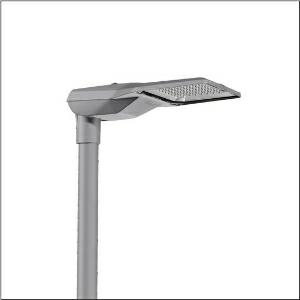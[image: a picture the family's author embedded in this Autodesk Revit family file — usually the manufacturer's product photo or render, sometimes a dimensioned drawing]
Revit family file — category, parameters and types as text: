
# Revit family: streetlight_sl_21_midi___stw1_0a_5xe3e43s08lb_9506
name_source: partatom
category: Lighting Fixtures
units: mm (PartAtom-declared; Revit-internal decimal feet)

## family parameters
Cut with Voids When Loaded = No
Host = Face
Light Source = No
Part Type = Normal
Room Calculation Point = No
Round Connector Dimension = Use Diameter
Shared = No

## types (1)
- --- (1 x LED, 14950 lm, 99.6 W, 4000K)
    Apparent Load = 100 VA
    CIE Flux Codes = 38 75 98 100 100
    Color Rendering = 70
    Color Temperature = 4000K
    Default Elevation = 1800 mm
    Description = Streetlight SL 21 midi, mast luminaire, primary light control with lens, of PMMA, primary optical cover: cover, of toughened safety glass, transparent, light distribution: STW1.0a, light emission: direct distribution, primary light characteristic: asymmetric, installation type: side-entry, post-top, LED, High Power LED, rated luminous flux: 14.950lm, luminous efficacy: 150lm/W, light colour: 740, colour temperature: 4000K, control gear: D4i, control: overheat protection, constant luminous flux control, time-dependent luminous flux control, flexible luminous flux parameterisation, pre-setting: logarithmic dimming characteristic, mains connection: 230..240V, AC, 50/60Hz, start of lifetime: 100W, end of service life: 102W, reduction: 46W, luminaire housing, of diecast aluminium, powder-coated, SITECO metallic grey (DB 702S), corrosivity category C5 high according to DIN EN ISO 12944, please order mast flange separately, inclination adjustable: 0°, 5°, 10°, 15°, sealing non-destructively replaceable, multi-level sealing system, length: 644mm, width: 335mm, height: 110mm, mast flange for spigot size: 42mm (side-entry): 5XC10008XM4, 60/48mm (side-entry/post-top): 5XC10108XM2, 76/60mm (side-entry/post-top): 5XC10108XM1, mounting height: 4..8m, Smart Interface above, protection rating (complete): IP66, insulation class (complete): insulation class II (safety insulation), certification: CE, ENEC, ENEC+, VDE, impact resistance: IK10, permissible operating ambient temperature for outdoor applications: -40..+50°C, standard-compliant lighting for roads and squares, packaging unit: 1 piece

Light Distribution: STW1.0a
    Height = 111 mm
    Lamp = 1 x LED
    Lamp Light Flux = 14950 lm
    Lamp Power = 99.6 W
    Lamp count = 1
    Length = 644 mm
    Luminous efficacy = 150 lm/W
    Manufacturer = Siteco
    ModVariant = No
    Model = 5XE3E43S08LB
    Number of Poles = 1
    OnlyDefault = Yes
    Power Factor = 1
    Product Name = Streetlight SL 21 midi | STW1.0a
    Product group = mast luminaire | pylon top
    ProductGroupID = 6100
    Protection Class = Protection class II
    Protection Degree = IP 66
    RLX_Detail_Level = 1
    RLX_Emergency_Light_Flux = 0 lm
    RLX_Emergency_Type = 0
    RLX_Emergency_Type_DB = No
    RlxData = <blob elided: 26789 chars, md5=908599d3>
    Socket = socket
    Standby Power = 0 W
    System Light Flux = 14950 lm
    System Power = 100 W
    Type Comments = factory setting: luminous flux: 100 % | dim-lin: 254 | 1020 mA
    Type Image = l_1004302.jpg
    URL = http://relux.com
    VarID = @adj_031615
    Voltage = 0 V
    Weight = 0.00 kg
    Width = 336 mm

## geometry (parser evidence)
native form markers: Blend x4, Sweep x12
no freeform markers — native parametric forms only
